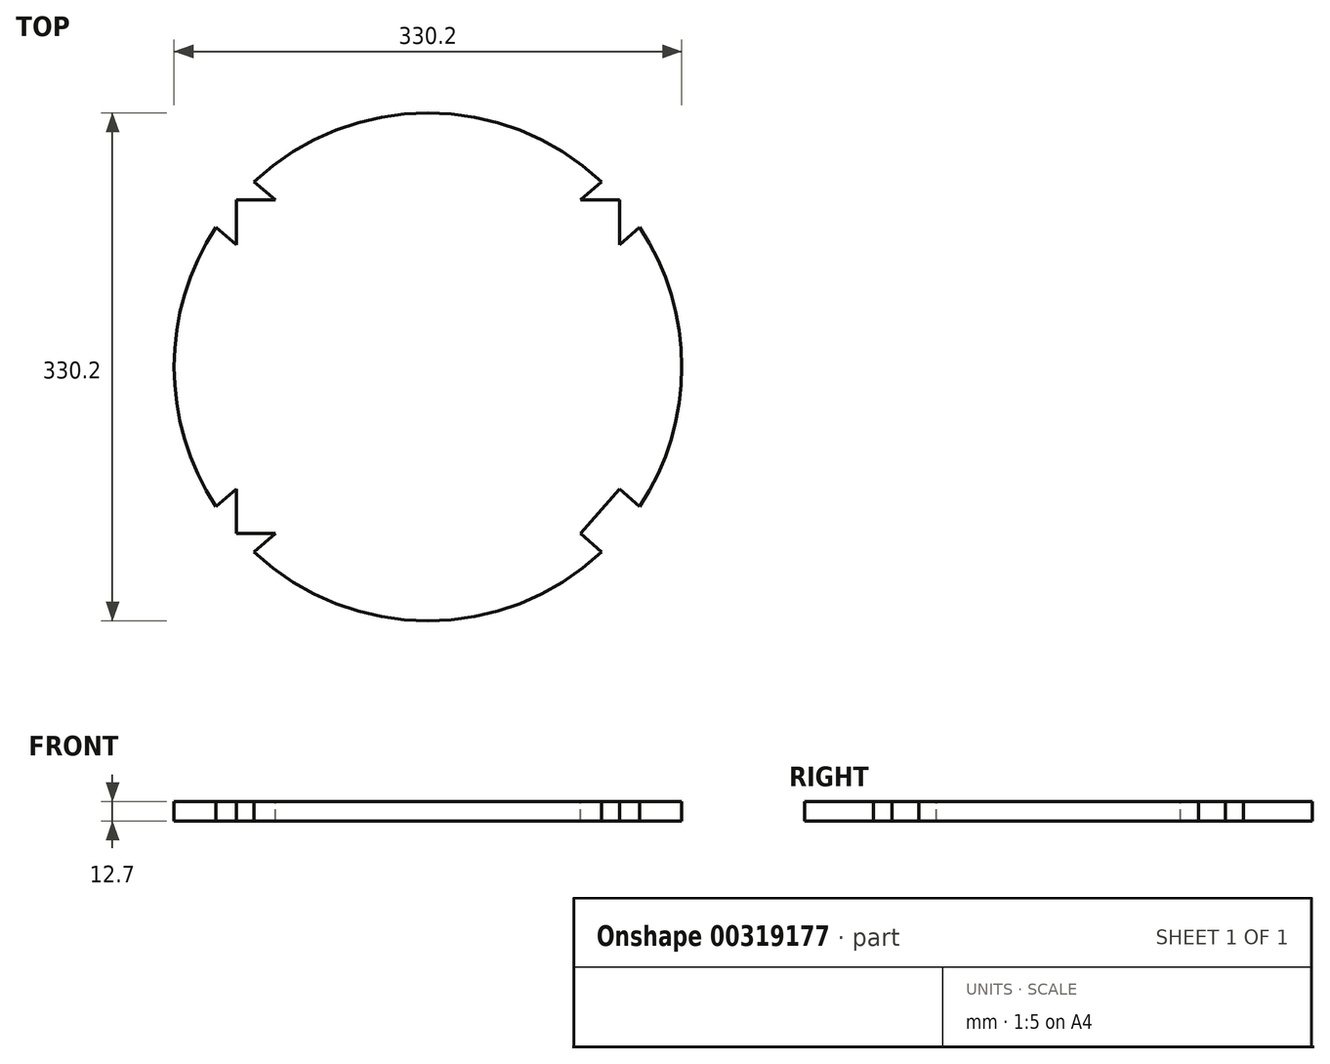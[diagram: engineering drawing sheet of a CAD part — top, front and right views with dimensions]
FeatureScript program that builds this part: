
annotation { "Feature Type Name" : "Feature", "Feature Type Description" : "" }
export const myFeature = defineFeature(function(context is Context, id is Id, definition is map)
    precondition{}
    {
        {
            var Q0;
            Q0=qCreatedBy(makeId("Top.planeOp"),FACE);
            var sketch = newSketch(context, id + "F0", { "sketchPlane" : qUnion([Q0])});
            skCircle(sketch, "E0", {"center": v(0, 0) * mm, "radius": 165.1 * mm});
            skSolve(sketch);
        }
        {
            var Q0;
            Q0=makeQuery(id+"F0.imprint","IMPRINT",FACE,{"disambiguationData":[TD([[makeQuery(id+"F0.imprint","IMPRINT",EDGE,{"derivedFrom":sQuery(id+"F0.wireOp",EDGE,"E0")}),1.0]])]});
            extrude(context, id + "F1", {"entities" : qUnion([Q0]), "depth" : 12.7 * mm});
        }
        {
            var Q0;
            Q0=makeQuery(id+"F1.opExtrude","CAP_FACE",FACE,{"disambiguationData":[OSD([sQuery(id+"F0.wireOp",EDGE,"E0")])],"isStart":false});
            var sketch = newSketch(context, id + "F2", { "sketchPlane" : qUnion([Q0])});
            skLineSegment(sketch, "E1.bottom", {"start": v(-124.54, 108.39) * mm, "end": v(124.54, 108.39) * mm});
            skLineSegment(sketch, "E1.top", {"start": v(-124.54, -108.39) * mm, "end": v(124.54, -108.39) * mm});
            skLineSegment(sketch, "E1.left", {"start": v(-124.54, 108.39) * mm, "end": v(-124.54, -108.39) * mm});
            skLineSegment(sketch, "E1.right", {"start": v(124.54, 108.39) * mm, "end": v(124.54, -108.39) * mm});
            skPoint(sketch, "E1.middle", {"position": v(0, 0) * mm});
            skLineSegment(sketch, "E2", {"start": v(124.54, -108.39) * mm, "end": v(110.17, -95.88) * mm});
            skLineSegment(sketch, "E3", {"start": v(110.17, -95.88) * mm, "end": v(124.54, -79.37) * mm});
            skLineSegment(sketch, "E4", {"start": v(110.17, -95.88) * mm, "end": v(99.28, -108.39) * mm});
            skLineSegment(sketch, "E5", {"start": v(-124.54, 108.39) * mm, "end": v(-110.17, 95.88) * mm});
            skLineSegment(sketch, "E6", {"start": v(-110.17, 95.88) * mm, "end": v(-99.28, 108.39) * mm});
            skLineSegment(sketch, "E7", {"start": v(-110.17, 95.88) * mm, "end": v(-124.54, 79.37) * mm});
            skLineSegment(sketch, "E8", {"start": v(-124.54, -108.39) * mm, "end": v(-110.17, -95.88) * mm});
            skLineSegment(sketch, "E9", {"start": v(-110.17, -95.88) * mm, "end": v(-124.54, -79.37) * mm});
            skLineSegment(sketch, "E10", {"start": v(-110.17, -95.88) * mm, "end": v(-99.28, -108.39) * mm});
            skLineSegment(sketch, "E11", {"start": v(110.17, 95.88) * mm, "end": v(124.54, 108.39) * mm});
            skLineSegment(sketch, "E12", {"start": v(124.54, 108.39) * mm, "end": v(110.17, 95.88) * mm});
            skLineSegment(sketch, "E13", {"start": v(110.17, 95.88) * mm, "end": v(99.28, 108.39) * mm});
            skLineSegment(sketch, "E14", {"start": v(110.17, 95.88) * mm, "end": v(124.54, 79.37) * mm});
            skLineSegment(sketch, "E15", {"start": v(99.28, 108.39) * mm, "end": v(113.02, 120.35) * mm});
            skLineSegment(sketch, "E16", {"start": v(124.54, 79.37) * mm, "end": v(137.8, 90.92) * mm});
            skLineSegment(sketch, "E17", {"start": v(-99.28, 108.39) * mm, "end": v(-113.02, 120.35) * mm});
            skLineSegment(sketch, "E18", {"start": v(-124.54, 79.37) * mm, "end": v(-137.8, 90.92) * mm});
            skLineSegment(sketch, "E19", {"start": v(-124.54, -79.37) * mm, "end": v(-137.8, -90.92) * mm});
            skLineSegment(sketch, "E20", {"start": v(-99.28, -108.39) * mm, "end": v(-113.02, -120.35) * mm});
            skLineSegment(sketch, "E21", {"start": v(99.28, -108.39) * mm, "end": v(113.02, -120.35) * mm});
            skLineSegment(sketch, "E22", {"start": v(124.54, -79.37) * mm, "end": v(137.8, -90.92) * mm});
            skLineSegment(sketch, "E23", {"start": v(-99.28, 108.39) * mm, "end": v(-110.17, 95.88) * mm});
            skSolve(sketch);
        }
        {
            var Q0;
            {var subQ3=sQuery(id+"F2.wireOp",EDGE,"E22");Q0=makeQuery(id+"F2.imprint","IMPRINT",FACE,{"disambiguationData":[TD([[makeQuery(id+"F2.imprint","IMPRINT",EDGE,{"derivedFrom":subQ3}),-1.0]])]});}
            var Q1;
            {var subQ0=sQuery(id+"F2.wireOp",EDGE,"E2");Q1=makeQuery(id+"F2.imprint","IMPRINT",FACE,{"disambiguationData":[TD([[makeQuery(id+"F2.imprint","IMPRINT",EDGE,{"derivedFrom":subQ0}),-1.0]])]});}
            var Q2;
            {var subQ0=sQuery(id+"F2.wireOp",EDGE,"E2");Q2=makeQuery(id+"F2.imprint","IMPRINT",FACE,{"disambiguationData":[TD([[makeQuery(id+"F2.imprint","IMPRINT",EDGE,{"derivedFrom":subQ0}),1.0]])]});}
            var Q3;
            {var subQ3=sQuery(id+"F2.wireOp",EDGE,"E21");Q3=makeQuery(id+"F2.imprint","IMPRINT",FACE,{"disambiguationData":[TD([[makeQuery(id+"F2.imprint","IMPRINT",EDGE,{"derivedFrom":subQ3}),1.0]])]});}
            var Q4;
            {var subQ3=sQuery(id+"F2.wireOp",EDGE,"E20");Q4=makeQuery(id+"F2.imprint","IMPRINT",FACE,{"disambiguationData":[TD([[makeQuery(id+"F2.imprint","IMPRINT",EDGE,{"derivedFrom":subQ3}),-1.0]])]});}
            var Q5;
            {var subQ0=sQuery(id+"F2.wireOp",EDGE,"E8");Q5=makeQuery(id+"F2.imprint","IMPRINT",FACE,{"disambiguationData":[TD([[makeQuery(id+"F2.imprint","IMPRINT",EDGE,{"derivedFrom":subQ0}),-1.0]])]});}
            var Q6;
            {var subQ0=sQuery(id+"F2.wireOp",EDGE,"E8");Q6=makeQuery(id+"F2.imprint","IMPRINT",FACE,{"disambiguationData":[TD([[makeQuery(id+"F2.imprint","IMPRINT",EDGE,{"derivedFrom":subQ0}),1.0]])]});}
            var Q7;
            {var subQ3=sQuery(id+"F2.wireOp",EDGE,"E19");Q7=makeQuery(id+"F2.imprint","IMPRINT",FACE,{"disambiguationData":[TD([[makeQuery(id+"F2.imprint","IMPRINT",EDGE,{"derivedFrom":subQ3}),1.0]])]});}
            var Q8;
            {var subQ0=sQuery(id+"F2.wireOp",EDGE,"E5");Q8=makeQuery(id+"F2.imprint","IMPRINT",FACE,{"disambiguationData":[TD([[makeQuery(id+"F2.imprint","IMPRINT",EDGE,{"derivedFrom":subQ0}),-1.0]])]});}
            var Q9;
            {var subQ3=sQuery(id+"F2.wireOp",EDGE,"E18");Q9=makeQuery(id+"F2.imprint","IMPRINT",FACE,{"disambiguationData":[TD([[makeQuery(id+"F2.imprint","IMPRINT",EDGE,{"derivedFrom":subQ3}),-1.0]])]});}
            var Q10;
            {var subQ0=sQuery(id+"F2.wireOp",EDGE,"E5");Q10=makeQuery(id+"F2.imprint","IMPRINT",FACE,{"disambiguationData":[TD([[makeQuery(id+"F2.imprint","IMPRINT",EDGE,{"derivedFrom":subQ0}),1.0]])]});}
            var Q11;
            {var subQ3=sQuery(id+"F2.wireOp",EDGE,"E17");Q11=makeQuery(id+"F2.imprint","IMPRINT",FACE,{"disambiguationData":[TD([[makeQuery(id+"F2.imprint","IMPRINT",EDGE,{"derivedFrom":subQ3}),1.0]])]});}
            var Q12;
            {var subQ0=sQuery(id+"F2.wireOp",EDGE,"E12");Q12=makeQuery(id+"F2.imprint","IMPRINT",FACE,{"disambiguationData":[TD([[makeQuery(id+"F2.imprint","IMPRINT",EDGE,{"derivedFrom":subQ0}),-1.0]])]});}
            var Q13;
            {var subQ3=sQuery(id+"F2.wireOp",EDGE,"E15");Q13=makeQuery(id+"F2.imprint","IMPRINT",FACE,{"disambiguationData":[TD([[makeQuery(id+"F2.imprint","IMPRINT",EDGE,{"derivedFrom":subQ3}),-1.0]])]});}
            var Q14;
            {var subQ0=sQuery(id+"F2.wireOp",EDGE,"E12");Q14=makeQuery(id+"F2.imprint","IMPRINT",FACE,{"disambiguationData":[TD([[makeQuery(id+"F2.imprint","IMPRINT",EDGE,{"derivedFrom":subQ0}),1.0]])]});}
            var Q15;
            {var subQ3=sQuery(id+"F2.wireOp",EDGE,"E16");Q15=makeQuery(id+"F2.imprint","IMPRINT",FACE,{"disambiguationData":[TD([[makeQuery(id+"F2.imprint","IMPRINT",EDGE,{"derivedFrom":subQ3}),1.0]])]});}
            extrude(context, id + "F3", {"entities" : qUnion([Q0, Q1, Q2, Q3, Q4, Q5, Q6, Q7, Q8, Q9, Q10, Q11, Q12, Q13, Q14, Q15]), "operationType" : NewBodyOperationType.REMOVE, "oppositeDirection" : true, "depth" : 25.4 * mm});
        }
    });
